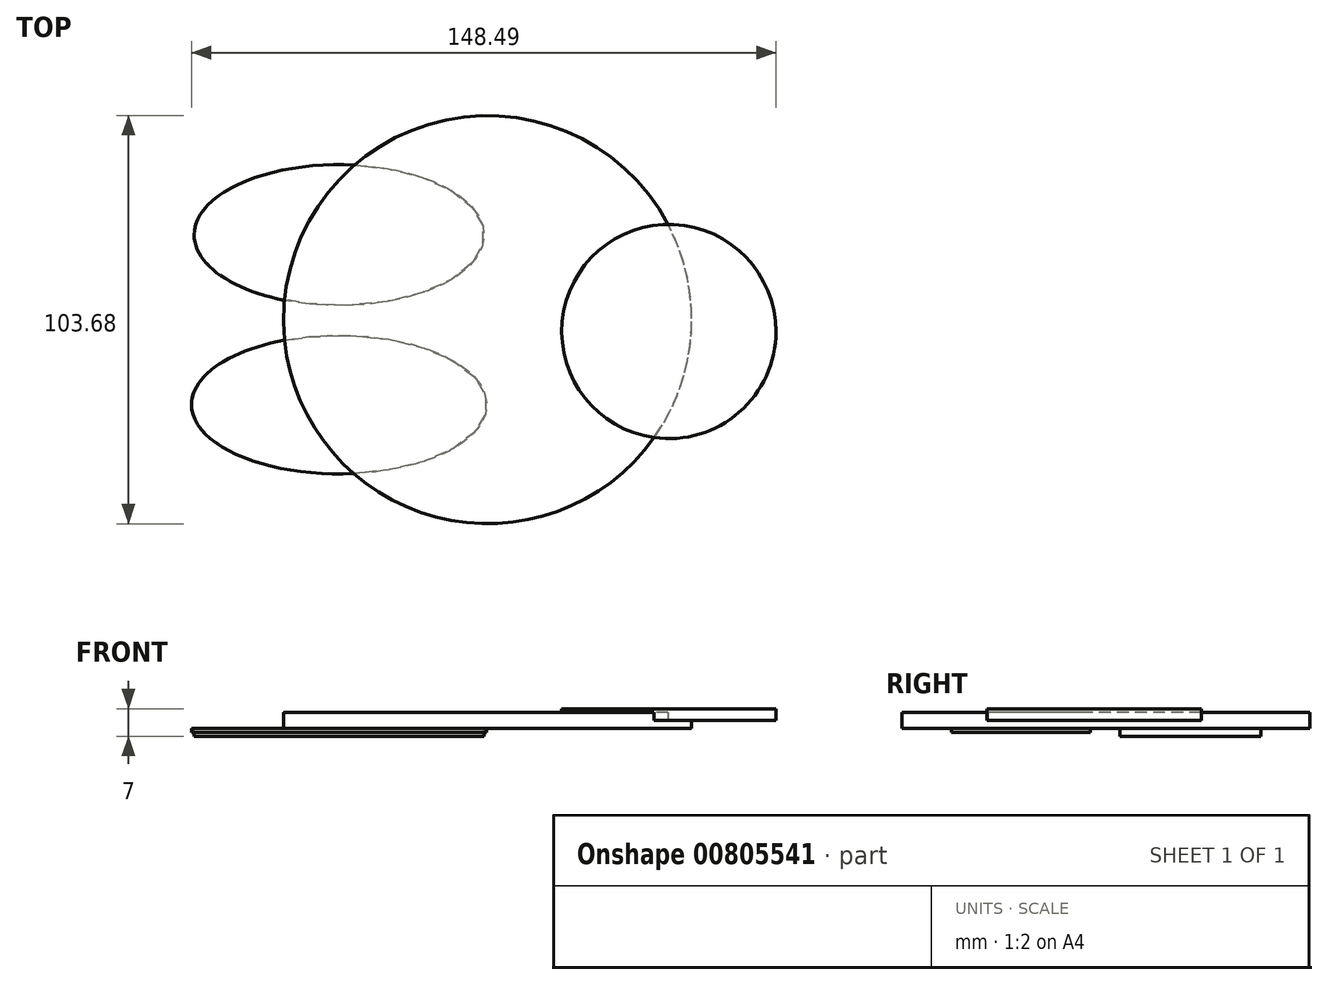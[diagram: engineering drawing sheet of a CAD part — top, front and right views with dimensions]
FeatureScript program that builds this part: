
annotation { "Feature Type Name" : "Feature", "Feature Type Description" : "" }
export const myFeature = defineFeature(function(context is Context, id is Id, definition is map)
    precondition{}
    {
        {
            var Q0;
            Q0=qCreatedBy(makeId("Top.planeOp"),FACE);
            var sketch = newSketch(context, id + "F0", { "sketchPlane" : qUnion([Q0])});
            skCircle(sketch, "E0", {"center": v(0, 0) * mm, "radius": 51.84 * mm});
            skSolve(sketch);
        }
        {
            var Q0;
            Q0=makeQuery(id+"F0.imprint","IMPRINT",FACE,{"disambiguationData":[TD([[makeQuery(id+"F0.imprint","IMPRINT",EDGE,{"derivedFrom":sQuery(id+"F0.wireOp",EDGE,"E0")}),1.0]])]});
            extrude(context, id + "F1", {"entities" : qUnion([Q0]), "depth" : 2 * mm, "offsetDistance" : 25 * mm});
        }
        {
            var Q0;
            Q0=makeQuery(id+"F1.opExtrude","CAP_FACE",FACE,{"disambiguationData":[OSD([sQuery(id+"F0.wireOp",EDGE,"E0")])],"isStart":true});
            var sketch = newSketch(context, id + "F2", { "sketchPlane" : qUnion([Q0])});
            skEllipse(sketch, "E1", {"center": v(-37.74, -21.5) * mm, "majorRadius": 36.83 * mm, "minorRadius": 17.9 * mm, "majorAxis": v(-1, 0)});
            skSolve(sketch);
        }
        {
            var Q0;
            Q0 = qSketchRegion(id + "F2", true);
            var Q1;
            Q1=makeQuery(id+"F5.imprint","IMPRINT",FACE,{"disambiguationData":[TD([[makeQuery(id+"F5.imprint","IMPRINT",EDGE,{"derivedFrom":makeQuery(id+"F1.opExtrude","CAP_EDGE",EDGE,{"disambiguationData":[OSD([sQuery(id+"F0.wireOp",EDGE,"E0")])],"isStart":false})}),1.0]])]});
            extrude(context, id + "F3", {"entities" : qUnion([Q0, Q1]), "depth" : 1 * mm, "offsetDistance" : 25 * mm});
        }
        {
            var Q0;
            Q0=makeQuery(id+"F3.opExtrude","CAP_FACE",FACE,{"disambiguationData":[OSD([sQuery(id+"F2.wireOp",EDGE,"E1")])],"isStart":false});
            var Q1;
            Q1=makeQuery(id+"F1.opExtrude","CAP_FACE",FACE,{"disambiguationData":[OSD([sQuery(id+"F0.wireOp",EDGE,"E0")])],"isStart":false});
            extrude(context, id + "F4", {"entities" : qUnion([Q0, Q1]), "operationType" : NewBodyOperationType.ADD, "depth" : 1 * mm, "offsetDistance" : 25 * mm});
        }
        {
            var Q0;
            Q0=makeQuery(id+"FTCburYuStgUCxD_1.boolean.opBoolean","MERGE",FACE,{"derivedFrom":[makeQuery(id+"F1.opExtrude","CAP_FACE",FACE,{"disambiguationData":[OSD([sQuery(id+"F0.wireOp",EDGE,"E0")])],"isStart":false}),makeQuery(id+"FTCburYuStgUCxD_1.opExtrude","CAP_FACE",FACE,{"disambiguationData":[OSD([sQuery(id+"FWH8Ttw59yBPMKB_1.wireOp",EDGE,"iucmYOde-83hm-1Iod-LmJx-Y4W3tn7ufyUU")])],"isStart":false})]});
            var sketch = newSketch(context, id + "F5", { "sketchPlane" : qUnion([Q0])});
            skCircle(sketch, "E2", {"center": v(0, 0) * mm, "radius": 52.32 * mm});
            skSolve(sketch);
        }
        {
            var Q0;
            Q0=makeQuery(id+"F1.opExtrude","CAP_FACE",FACE,{"disambiguationData":[OSD([sQuery(id+"F0.wireOp",EDGE,"E0")])],"isStart":true});
            var sketch = newSketch(context, id + "F6", { "sketchPlane" : qUnion([Q0])});
            skEllipse(sketch, "E3", {"center": v(-37.74, 21.58) * mm, "majorRadius": 37.51 * mm, "minorRadius": 17.63 * mm, "majorAxis": v(-1, 0)});
            skPoint(sketch, "E3.centerSnap0", {"position": v(-37.74, -3.6) * mm});
            skSolve(sketch);
        }
        {
            var Q0;
            Q0 = qSketchRegion(id + "F6", true);
            extrude(context, id + "F7", {"entities" : qUnion([Q0]), "operationType" : NewBodyOperationType.ADD, "depth" : 1 * mm, "offsetDistance" : 25 * mm});
        }
        {
            var Q0;
            Q0=makeQuery(id+"F5.imprint","IMPRINT",FACE,{"disambiguationData":[TD([[makeQuery(id+"F5.imprint","IMPRINT",EDGE,{"derivedFrom":makeQuery(id+"F1.opExtrude","CAP_EDGE",EDGE,{"disambiguationData":[OSD([sQuery(id+"F0.wireOp",EDGE,"E0")])],"isStart":false})}),1.0]])]});
            var sketch = newSketch(context, id + "F8", { "sketchPlane" : qUnion([Q0])});
            skSolve(sketch);
        }
        {
            var Q0;
            Q0=makeQuery(id+"F5.imprint","IMPRINT",FACE,{"disambiguationData":[TD([[makeQuery(id+"F5.imprint","IMPRINT",EDGE,{"derivedFrom":makeQuery(id+"F1.opExtrude","CAP_EDGE",EDGE,{"disambiguationData":[OSD([sQuery(id+"F0.wireOp",EDGE,"E0")])],"isStart":false})}),1.0]])]});
            var sketch = newSketch(context, id + "F9", { "sketchPlane" : qUnion([Q0])});
            skArc(sketch, "E4", {"start": v(-12.8, -35.17) * mm, "mid": v(-7.45, -19.77) * mm, "end": v(6.56, -11.44) * mm});
            skSolve(sketch);
        }
        {
            var Q0;
            Q0=sQuery(id+"F9.wireOp",EDGE,"E4");
            extrude(context, id + "F10", {"bodyType" : ToolBodyType.SURFACE, "surfaceEntities" : qUnion([Q0]), "depth" : 1 * mm, "offsetDistance" : 25 * mm});
        }
        {
            var Q0;
            Q0=makeQuery(id+"F5.imprint","IMPRINT",FACE,{"disambiguationData":[TD([[makeQuery(id+"F5.imprint","IMPRINT",EDGE,{"derivedFrom":makeQuery(id+"F1.opExtrude","CAP_EDGE",EDGE,{"disambiguationData":[OSD([sQuery(id+"F0.wireOp",EDGE,"E0")])],"isStart":false})}),1.0]])]});
            var sketch = newSketch(context, id + "F11", { "sketchPlane" : qUnion([Q0])});
            skArc(sketch, "E5", {"start": v(0, 37) * mm, "mid": v(-0.05, 20.04) * mm, "end": v(13.49, 9.83) * mm});
            skSolve(sketch);
        }
        {
            var Q0;
            Q0 = qSketchRegion(id + "F11", true);
            var Q1;
            Q1=makeQuery(id+"F8.imprint","IMPRINT",FACE,{"disambiguationData":[TD([[makeQuery(id+"F8.imprint","IMPRINT",EDGE,{"derivedFrom":makeQuery(id+"F5.imprint","IMPRINT",EDGE,{"derivedFrom":makeQuery(id+"F1.opExtrude","CAP_EDGE",EDGE,{"disambiguationData":[OSD([sQuery(id+"F0.wireOp",EDGE,"E0")])],"isStart":false})})}),1.0]])]});
            var Q2;
            Q2=sQuery(id+"F11.wireOp",EDGE,"E5");
            extrude(context, id + "F12", {"entities" : qUnion([Q0, Q1]), "bodyType" : ToolBodyType.SURFACE, "surfaceEntities" : qUnion([Q2]), "depth" : 1 * mm, "offsetDistance" : 25 * mm});
        }
        {
            var Q0;
            Q0=makeQuery(id+"F1.opExtrude","CAP_FACE",FACE,{"disambiguationData":[OSD([sQuery(id+"F0.wireOp",EDGE,"E0")])],"isStart":false});
            var sketch = newSketch(context, id + "F13", { "sketchPlane" : qUnion([Q0])});
            skCircle(sketch, "E6", {"center": v(46.03, -3) * mm, "radius": 27.2 * mm});
            skSolve(sketch);
        }
        {
            var Q0;
            {var subQ0=sQuery(id+"F13.wireOp",EDGE,"E6");var subQ1=makeQuery(id+"F1.opExtrude","CAP_EDGE",EDGE,{"disambiguationData":[OSD([sQuery(id+"F0.wireOp",EDGE,"E0")])],"isStart":false});var subQ2=makeQuery(id+"F13.imprint","INTERSECT",VERTEX,{"disambiguationData":[OD(0.0)],"derivedFrom":[subQ1,subQ0]});Q0=makeQuery(id+"F13.imprint","IMPRINT",FACE,{"disambiguationData":[TD([[makeQuery(id+"F13.imprint","IMPRINT",EDGE,{"disambiguationData":[TD([[subQ2,1.0]])],"derivedFrom":subQ0}),1.0]])]});}
            var Q1;
            {var subQ0=sQuery(id+"F13.wireOp",EDGE,"E6");var subQ1=makeQuery(id+"F1.opExtrude","CAP_EDGE",EDGE,{"disambiguationData":[OSD([sQuery(id+"F0.wireOp",EDGE,"E0")])],"isStart":false});var subQ2=makeQuery(id+"F13.imprint","INTERSECT",VERTEX,{"disambiguationData":[OD(0.0)],"derivedFrom":[subQ1,subQ0]});Q1=makeQuery(id+"F13.imprint","IMPRINT",FACE,{"disambiguationData":[TD([[makeQuery(id+"F13.imprint","IMPRINT",EDGE,{"disambiguationData":[TD([[subQ2,-1.0]])],"derivedFrom":subQ0}),1.0]])]});}
            extrude(context, id + "F14", {"entities" : qUnion([Q0, Q1]), "operationType" : NewBodyOperationType.ADD, "depth" : 1 * mm, "offsetDistance" : 25 * mm});
        }
        {
            var Q0;
            Q0=makeQuery(id+"F14.opExtrude","CAP_FACE",FACE,{"disambiguationData":[OSD([sQuery(id+"F13.wireOp",EDGE,"E6")])],"isStart":false});
            var Q1;
            Q1=makeQuery(id+"F5.imprint","IMPRINT",FACE,{"disambiguationData":[TD([[makeQuery(id+"F5.imprint","IMPRINT",EDGE,{"derivedFrom":makeQuery(id+"F1.opExtrude","CAP_EDGE",EDGE,{"disambiguationData":[OSD([sQuery(id+"F0.wireOp",EDGE,"E0")])],"isStart":false})}),1.0]])]});
            extrude(context, id + "F15", {"entities" : qUnion([Q0, Q1]), "operationType" : NewBodyOperationType.ADD, "depth" : 2 * mm, "offsetDistance" : 25 * mm});
        }
    });
